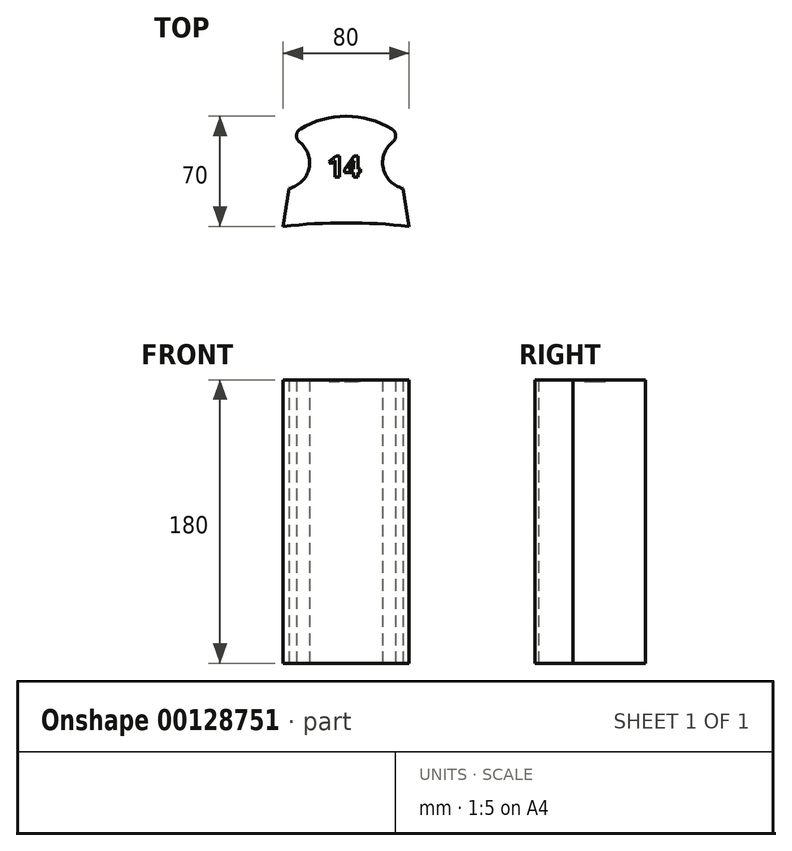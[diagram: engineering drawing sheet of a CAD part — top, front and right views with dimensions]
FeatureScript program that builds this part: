
annotation { "Feature Type Name" : "Feature", "Feature Type Description" : "" }
export const myFeature = defineFeature(function(context is Context, id is Id, definition is map)
    precondition{}
    {
        {
            var Q0;
            Q0=qCreatedBy(makeId("Top.planeOp"),FACE);
            var sketch = newSketch(context, id + "F0", { "sketchPlane" : qUnion([Q0])});
            skLineSegment(sketch, "E0", {"start": v(0, 0) * mm, "end": v(3.87, 24.16) * mm});
            skLineSegment(sketch, "E1", {"start": v(0, 0) * mm, "end": v(80, 0) * mm, "construction": true});
            skLineSegment(sketch, "E2", {"start": v(40, 0) * mm, "end": v(40, 70) * mm, "construction": true});
            skArc(sketch, "E3", {"start": v(3.87, 24.16) * mm, "mid": v(16.4, 36.85) * mm, "end": v(10.4, 53.64) * mm});
            skArc(sketch, "E4.MirrorCS", {"start": v(76.13, 24.16) * mm, "mid": v(63.6, 36.85) * mm, "end": v(69.6, 53.64) * mm});
            skLineSegment(sketch, "E5.MirrorCS", {"start": v(80, 0) * mm, "end": v(76.13, 24.16) * mm});
            skArc(sketch, "E6", {"start": v(69.1, 61.84) * mm, "mid": v(40, 70) * mm, "end": v(10.9, 61.84) * mm});
            skPoint(sketch, "E7.visualSharp", {"position": v(3.87, 56.79) * mm});
            skArc(sketch, "E7.filletArc", {"start": v(10.9, 61.84) * mm, "mid": v(8.5, 57.87) * mm, "end": v(10.4, 53.64) * mm});
            skPoint(sketch, "E8.visualSharp", {"position": v(76.13, 56.79) * mm});
            skArc(sketch, "E8.filletArc", {"start": v(69.6, 53.64) * mm, "mid": v(71.5, 57.87) * mm, "end": v(69.1, 61.84) * mm});
            skArc(sketch, "E9.MirrorCS", {"start": v(0, 0) * mm, "mid": v(40, 2.26) * mm, "end": v(80, 0) * mm});
            skSolve(sketch);
        }
        {
            var Q0;
            Q0=makeQuery(id+"F0.imprint","IMPRINT",FACE,{"disambiguationData":[TD([[makeQuery(id+"F0.imprint","IMPRINT",EDGE,{"derivedFrom":sQuery(id+"F0.wireOp",EDGE,"E0")}),-1.0]])]});
            extrude(context, id + "F1", {"entities" : qUnion([Q0]), "depth" : 180 * mm});
        }
        {
            var Q0;
            Q0=makeQuery(id+"F1.opExtrude","CAP_FACE",FACE,{"disambiguationData":[OSD([sQuery(id+"F0.wireOp",EDGE,"E0"),sQuery(id+"F0.wireOp",EDGE,"E3"),sQuery(id+"F0.wireOp",EDGE,"E4.MirrorCS"),sQuery(id+"F0.wireOp",EDGE,"E5.MirrorCS"),sQuery(id+"F0.wireOp",EDGE,"E6"),sQuery(id+"F0.wireOp",EDGE,"E7.filletArc"),sQuery(id+"F0.wireOp",EDGE,"E8.filletArc"),sQuery(id+"F0.wireOp",EDGE,"NzHJaS1e-Hx9R-e02U-jfAq-aO6yktXq1YBm")])],"isStart":false});
            var sketch = newSketch(context, id + "F2", { "sketchPlane" : qUnion([Q0])});
            skText(sketch, "E10", { "text": "14", "fontName": "OpenSans-Bold.ttf"});
            const initialGuessF2  = {"E10": [0.02808, 0.03137, 1, 0, 0.01349]};
            skSetInitialGuess(sketch, initialGuessF2);
            skSolve(sketch);
        }
        {
            var Q0;
            Q0=qSketchRegion(id+"F2",true);
            extrude(context, id + "F3", {"entities" : qUnion([Q0]), "operationType" : NewBodyOperationType.REMOVE, "oppositeDirection" : true, "depth" : 1 * mm});
        }
    });
